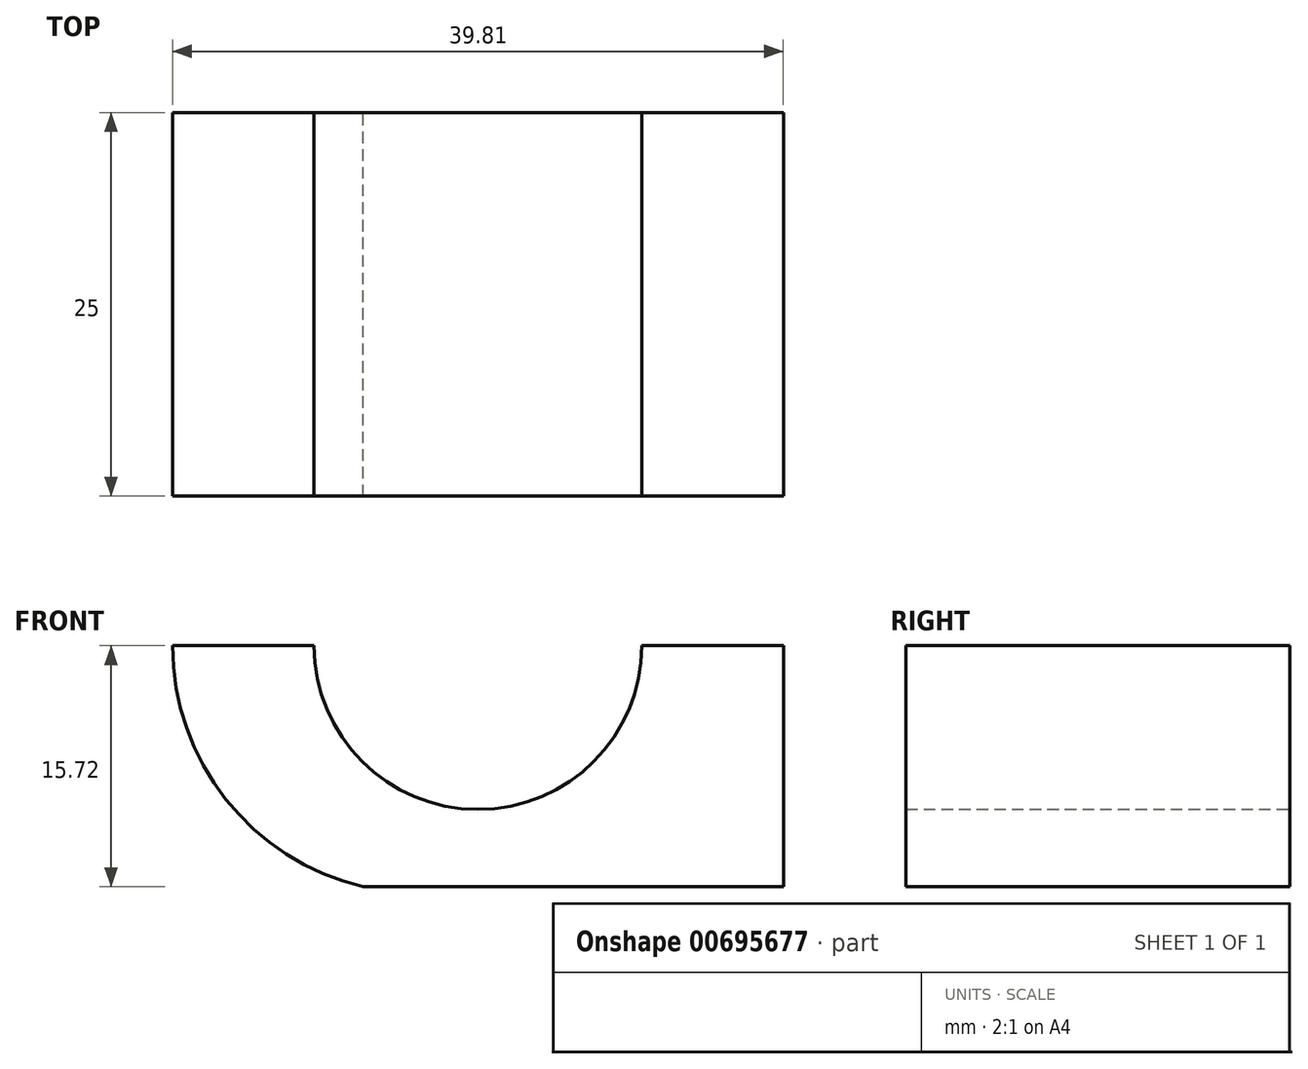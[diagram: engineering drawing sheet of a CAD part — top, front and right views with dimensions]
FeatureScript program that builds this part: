
annotation { "Feature Type Name" : "Feature", "Feature Type Description" : "" }
export const myFeature = defineFeature(function(context is Context, id is Id, definition is map)
    precondition{}
    {
        {
            var Q0;
            Q0=qCreatedBy(makeId("Front.planeOp"),FACE);
            var sketch = newSketch(context, id + "F0", { "sketchPlane" : qUnion([Q0])});
            skLineSegment(sketch, "E0", {"start": v(-48.6, 15.72) * mm, "end": v(-39.38, 15.72) * mm});
            skLineSegment(sketch, "E1", {"start": v(-8.8, 15.72) * mm, "end": v(-8.8, 0) * mm});
            skLineSegment(sketch, "E2", {"start": v(-8.8, 0) * mm, "end": v(-36.19, 0) * mm});
            skArc(sketch, "E3", {"start": v(-39.38, 15.72) * mm, "mid": v(-28.7, 5.04) * mm, "end": v(-18.02, 15.72) * mm});
            skArc(sketch, "E4", {"start": v(-48.6, 15.72) * mm, "mid": v(-45.13, 5.7) * mm, "end": v(-36.19, 0) * mm});
            skLineSegment(sketch, "E5.trimOffspring", {"start": v(-18.02, 15.72) * mm, "end": v(-8.8, 15.72) * mm});
            skPoint(sketch, "E6.orphan", {"position": v(-48.6, 0) * mm});
            skPoint(sketch, "E7.orphan", {"position": v(-28.7, 0) * mm});
            skSolve(sketch);
        }
        {
            var Q0;
            Q0 = qSketchRegion(id + "F0", true);
            extrude(context, id + "F1", {"entities" : qUnion([Q0]), "depth" : 25 * mm, "offsetDistance" : 25 * mm});
        }
    });
